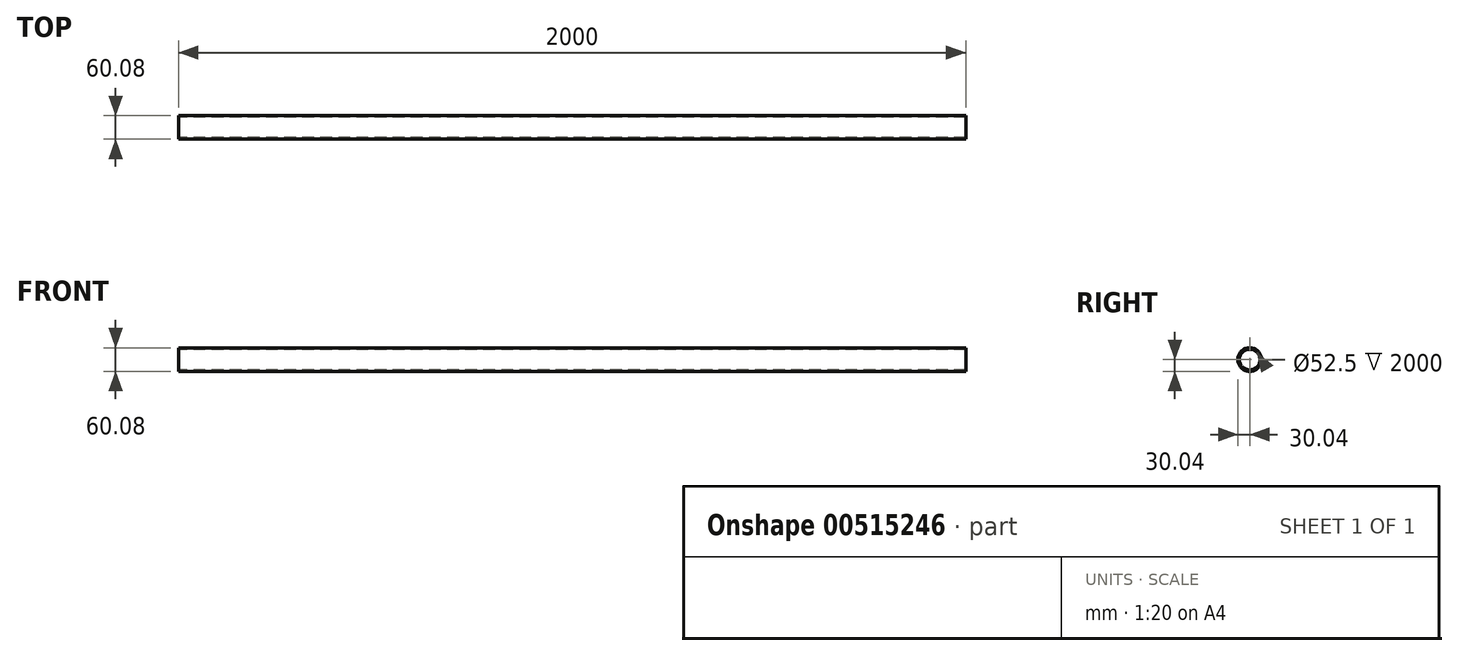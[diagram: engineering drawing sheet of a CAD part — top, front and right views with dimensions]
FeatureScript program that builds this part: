
annotation { "Feature Type Name" : "Feature", "Feature Type Description" : "" }
export const myFeature = defineFeature(function(context is Context, id is Id, definition is map)
    precondition{}
    {
        {
            var Q0;
            Q0=qCreatedBy(makeId("Right.planeOp"),FACE);
            var sketch = newSketch(context, id + "F0", { "sketchPlane" : qUnion([Q0])});
            skCircle(sketch, "E0", {"center": v(0, 0) * mm, "radius": 26.25 * mm});
            skCircle(sketch, "E1", {"center": v(0, 0) * mm, "radius": 30.04 * mm});
            skSolve(sketch);
        }
        {
            var Q0;
            Q0=makeQuery(id+"F0.imprint","IMPRINT",FACE,{"disambiguationData":[TD([[makeQuery(id+"F0.imprint","IMPRINT",EDGE,{"derivedFrom":sQuery(id+"F0.wireOp",EDGE,"E0")}),-1.0]])]});
            extrude(context, id + "F1", {"entities" : qUnion([Q0]), "depth" : 2000 * mm, "offsetDistance" : 25 * mm});
        }
    });
